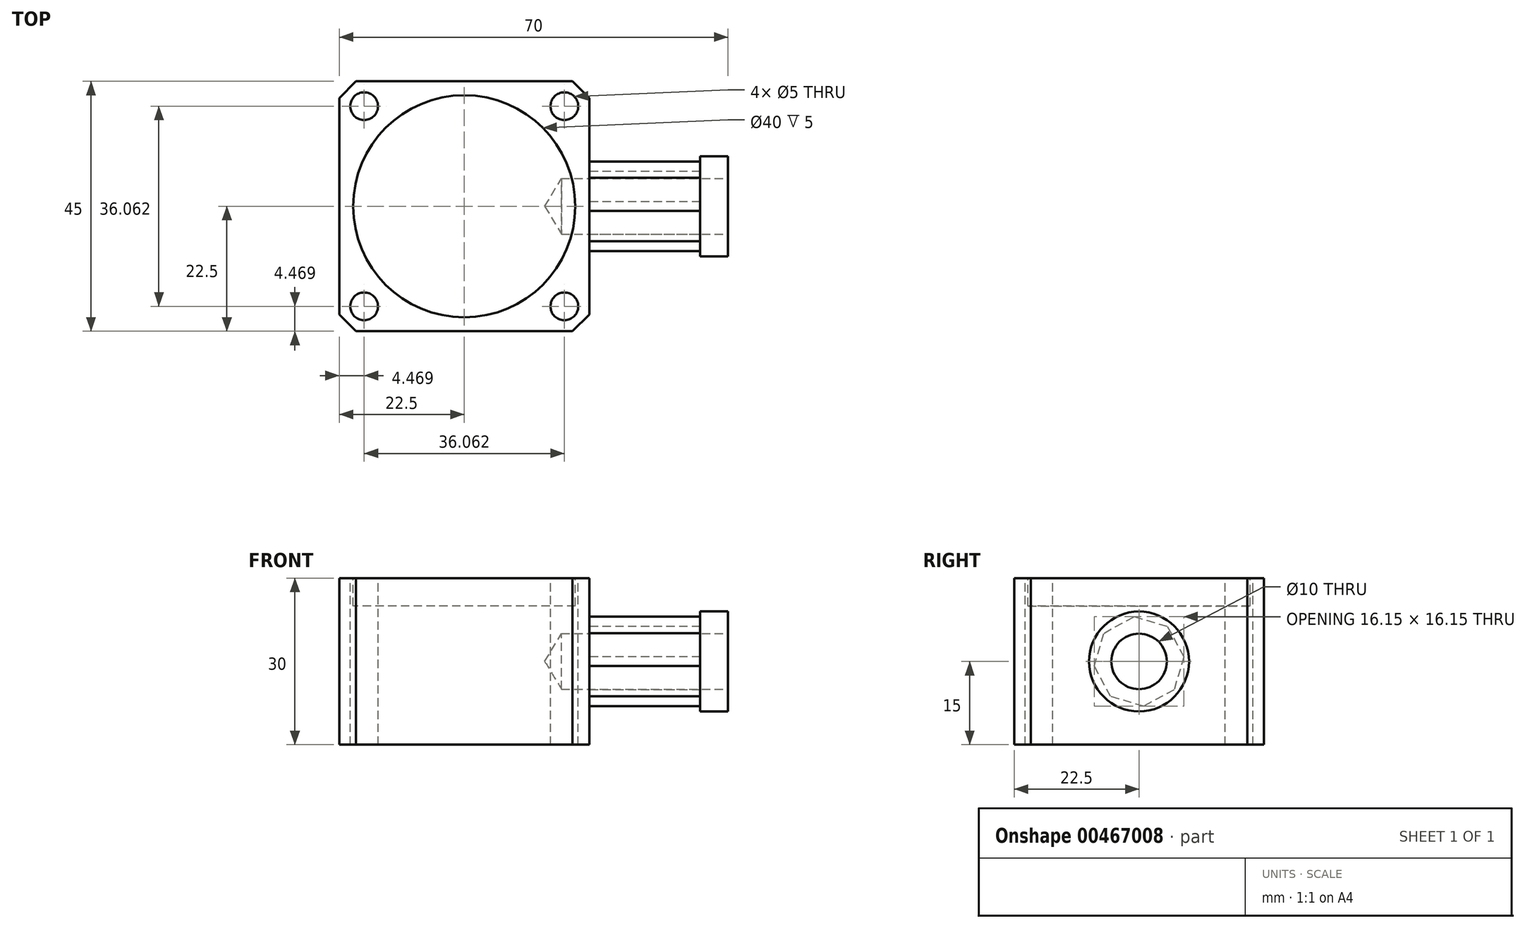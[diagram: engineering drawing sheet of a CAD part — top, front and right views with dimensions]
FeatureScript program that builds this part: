
annotation { "Feature Type Name" : "Feature", "Feature Type Description" : "" }
export const myFeature = defineFeature(function(context is Context, id is Id, definition is map)
    precondition{}
    {
        {
            var Q0;
            Q0=qCreatedBy(makeId("Top.planeOp"),FACE);
            var sketch = newSketch(context, id + "F0", { "sketchPlane" : qUnion([Q0])});
            skLineSegment(sketch, "E0.bottom", {"start": v(0, 0) * mm, "end": v(-45, 0) * mm});
            skLineSegment(sketch, "E0.top", {"start": v(0, -45) * mm, "end": v(-45, -45) * mm});
            skLineSegment(sketch, "E0.left", {"start": v(0, 0) * mm, "end": v(0, -45) * mm});
            skLineSegment(sketch, "E0.right", {"start": v(-45, 0) * mm, "end": v(-45, -45) * mm});
            skSolve(sketch);
        }
        {
            var Q0;
            Q0=makeQuery(id+"F0.imprint","IMPRINT",FACE,{"disambiguationData":[TD([[makeQuery(id+"F0.imprint","IMPRINT",EDGE,{"derivedFrom":sQuery(id+"F0.wireOp",EDGE,"E0.bottom")}),1.0]])]});
            extrude(context, id + "F1", {"entities" : qUnion([Q0]), "depth" : 30 * mm, "offsetDistance" : 25 * mm});
        }
        {
            var Q0;
            Q0=makeQuery(id+"F1.opExtrude","SWEPT_EDGE",EDGE,{"disambiguationData":[OSD([sQuery(id+"F0.wireOp",EDGE,"E0.top"),sQuery(id+"F0.wireOp",EDGE,"E0.right")])]});
            var Q1;
            Q1=makeQuery(id+"F1.opExtrude","SWEPT_EDGE",EDGE,{"disambiguationData":[OSD([sQuery(id+"F0.wireOp",EDGE,"E0.top"),sQuery(id+"F0.wireOp",EDGE,"E0.left")])]});
            var Q2;
            Q2=makeQuery(id+"F1.opExtrude","SWEPT_EDGE",EDGE,{"disambiguationData":[OSD([sQuery(id+"F0.wireOp",EDGE,"E0.bottom"),sQuery(id+"F0.wireOp",EDGE,"E0.left")])]});
            var Q3;
            Q3=makeQuery(id+"F1.opExtrude","SWEPT_EDGE",EDGE,{"disambiguationData":[OSD([sQuery(id+"F0.wireOp",EDGE,"E0.bottom"),sQuery(id+"F0.wireOp",EDGE,"E0.right")])]});
            chamfer(context, id + "F2", {"entities" : qUnion([Q0, Q1, Q2, Q3]), "width" : 3 * mm, "tangentPropagation" : true});
        }
        {
            var Q0;
            Q0=makeQuery(id+"F1.opExtrude","CAP_FACE",FACE,{"disambiguationData":[OSD([sQuery(id+"F0.wireOp",EDGE,"E0.bottom"),sQuery(id+"F0.wireOp",EDGE,"E0.top"),sQuery(id+"F0.wireOp",EDGE,"E0.left"),sQuery(id+"F0.wireOp",EDGE,"E0.right")])],"isStart":false});
            var sketch = newSketch(context, id + "F3", { "sketchPlane" : qUnion([Q0])});
            skLineSegment(sketch, "E1", {"start": v(-22.5, -22.5) * mm, "end": v(0, -22.5) * mm});
            skPoint(sketch, "E1.startSnap0", {"position": v(-22.5, -3) * mm});
            skPoint(sketch, "E1.startSnap1", {"position": v(0, -22.5) * mm});
            skLineSegment(sketch, "E2", {"start": v(0, -22.5) * mm, "end": v(-22.5, -22.5) * mm});
            skLineSegment(sketch, "E3", {"start": v(-22.5, -22.5) * mm, "end": v(-40.53, -40.53) * mm});
            skLineSegment(sketch, "E4.MirrorCS", {"start": v(-22.5, -22.5) * mm, "end": v(-40.53, -4.47) * mm});
            skPoint(sketch, "E5", {"position": v(-40.53, -40.53) * mm});
            skPoint(sketch, "E6", {"position": v(-40.53, -4.47) * mm});
            skLineSegment(sketch, "E7", {"start": v(-22.5, -22.5) * mm, "end": v(-4.47, -4.47) * mm});
            skLineSegment(sketch, "E8.MirrorCS", {"start": v(-22.5, -22.5) * mm, "end": v(-4.47, -40.53) * mm});
            skPoint(sketch, "E9", {"position": v(-4.47, -4.47) * mm});
            skPoint(sketch, "E10", {"position": v(-4.47, -40.53) * mm});
            skSolve(sketch);
        }
        {
            var Q0;
            Q0=sQuery(id+"F3.wireOp",VERTEX,"E5");
            var Q1;
            Q1=sQuery(id+"F3.wireOp",VERTEX,"E6");
            var Q2;
            Q2=sQuery(id+"F3.wireOp",VERTEX,"E9");
            var Q3;
            Q3=sQuery(id+"F3.wireOp",VERTEX,"E10");
            var Q4;
            Q4=makeQuery(id+"F1.opExtrude","SWEPT_BODY",BODY,{"disambiguationData":[OSD([sQuery(id+"F0.wireOp",EDGE,"E0.bottom"),sQuery(id+"F0.wireOp",EDGE,"E0.top"),sQuery(id+"F0.wireOp",EDGE,"E0.left"),sQuery(id+"F0.wireOp",EDGE,"E0.right")])]});
            hole(context, id + "F4", {"style" : HoleStyle.SIMPLE, "endStyle" : HoleEndStyle.THROUGH, "holeDiameter" : 5 * mm, "isTappedThrough" : true, "tappedDepth" : 12 * mm, "tapClearance" : 3, "locations" : qUnion([Q0, Q1, Q2, Q3]), "scope" : qUnion([Q4])});
        }
        {
            var Q0;
            Q0=makeQuery(id+"F1.opExtrude","SWEPT_FACE",FACE,{"disambiguationData":[OSD([sQuery(id+"F0.wireOp",EDGE,"E0.left")])]});
            var sketch = newSketch(context, id + "F5", { "sketchPlane" : qUnion([Q0])});
            skCircle(sketch, "E11", {"center": v(-22.5, 15) * mm, "radius": 7.5 * mm});
            skPoint(sketch, "E11.centerSnap0", {"position": v(-42, 15) * mm});
            skPoint(sketch, "E11.centerSnap1", {"position": v(-22.5, 30) * mm});
            skCircle(sketch, "E12.cCircle", {"center": v(-22.5, 15) * mm, "radius": 7.5 * mm, "construction": true});
            skLineSegment(sketch, "E12.0", {"start": v(-30.57, 14.16) * mm, "end": v(-28.8, 20.12) * mm});
            skLineSegment(sketch, "E12.1", {"start": v(-28.8, 20.12) * mm, "end": v(-23.34, 23.07) * mm});
            skLineSegment(sketch, "E12.2", {"start": v(-23.34, 23.07) * mm, "end": v(-17.38, 21.3) * mm});
            skLineSegment(sketch, "E12.3", {"start": v(-17.38, 21.3) * mm, "end": v(-14.43, 15.84) * mm});
            skLineSegment(sketch, "E12.4", {"start": v(-14.43, 15.84) * mm, "end": v(-16.2, 9.88) * mm});
            skLineSegment(sketch, "E12.5", {"start": v(-16.2, 9.88) * mm, "end": v(-21.66, 6.93) * mm});
            skLineSegment(sketch, "E12.6", {"start": v(-21.66, 6.93) * mm, "end": v(-27.62, 8.7) * mm});
            skLineSegment(sketch, "E12.7", {"start": v(-27.62, 8.7) * mm, "end": v(-30.57, 14.16) * mm});
            skPoint(sketch, "E12.0.midPoint", {"position": v(-29.69, 17.14) * mm});
            skSolve(sketch);
        }
        {
            var Q0;
            Q0 = qSketchRegion(id + "F5", true);
            extrude(context, id + "F6", {"entities" : qUnion([Q0]), "operationType" : NewBodyOperationType.ADD, "depth" : 20 * mm});
        }
        {
            var Q0;
            Q0=makeQuery(id+"F6.opExtrude","CAP_FACE",FACE,{"disambiguationData":[OSD([sQuery(id+"F5.wireOp",EDGE,"E12.0"),sQuery(id+"F5.wireOp",EDGE,"E12.1"),sQuery(id+"F5.wireOp",EDGE,"E12.2"),sQuery(id+"F5.wireOp",EDGE,"E12.3"),sQuery(id+"F5.wireOp",EDGE,"E12.4"),sQuery(id+"F5.wireOp",EDGE,"E12.5"),sQuery(id+"F5.wireOp",EDGE,"E12.6"),sQuery(id+"F5.wireOp",EDGE,"E12.7")])],"isStart":false});
            var sketch = newSketch(context, id + "F7", { "sketchPlane" : qUnion([Q0])});
            skLineSegment(sketch, "E13", {"start": v(-20.36, 22.19) * mm, "end": v(-24.64, 7.81) * mm});
            skLineSegment(sketch, "E14", {"start": v(-24.64, 7.81) * mm, "end": v(-29.69, 17.14) * mm});
            skLineSegment(sketch, "E15", {"start": v(-29.69, 17.14) * mm, "end": v(-15.31, 12.86) * mm});
            skCircle(sketch, "E16", {"center": v(-22.5, 15) * mm, "radius": 9 * mm});
            skSolve(sketch);
        }
        {
            var Q0;
            Q0 = qSketchRegion(id + "F7", true);
            var Q1;
            {var subQ0=sQuery(id+"F7.wireOp",EDGE,"E14");Q1=makeQuery(id+"F7.imprint","IMPRINT",FACE,{"disambiguationData":[TD([[makeQuery(id+"F7.imprint","IMPRINT",EDGE,{"derivedFrom":subQ0}),-1.0]])]});}
            extrude(context, id + "F8", {"entities" : qUnion([Q0, Q1]), "operationType" : NewBodyOperationType.ADD, "depth" : 5 * mm});
        }
        {
            var Q0;
            Q0=makeQuery(id+"F8.opExtrude","CAP_FACE",FACE,{"disambiguationData":[OSD([sQuery(id+"F7.wireOp",EDGE,"E16")])],"isStart":false});
            var sketch = newSketch(context, id + "F9", { "sketchPlane" : qUnion([Q0])});
            skPoint(sketch, "E17", {"position": v(-22.5, 15) * mm});
            skSolve(sketch);
        }
        {
            var Q0;
            Q0=sQuery(id+"F9.wireOp",VERTEX,"E17");
            var Q1;
            Q1=makeQuery(id+"F1.opExtrude","SWEPT_BODY",BODY,{"disambiguationData":[OSD([sQuery(id+"F0.wireOp",EDGE,"E0.bottom"),sQuery(id+"F0.wireOp",EDGE,"E0.top"),sQuery(id+"F0.wireOp",EDGE,"E0.left"),sQuery(id+"F0.wireOp",EDGE,"E0.right")])]});
            hole(context, id + "F10", {"style" : HoleStyle.SIMPLE, "endStyle" : HoleEndStyle.BLIND, "holeDiameter" : 10 * mm, "holeDepth" : 30 * mm, "isTappedThrough" : true, "tappedDepth" : 12 * mm, "tapClearance" : 3, "locations" : qUnion([Q0]), "scope" : qUnion([Q1])});
        }
        {
            var Q0;
            Q0=makeQuery(id+"F1.opExtrude","CAP_FACE",FACE,{"disambiguationData":[OSD([sQuery(id+"F0.wireOp",EDGE,"E0.bottom"),sQuery(id+"F0.wireOp",EDGE,"E0.top"),sQuery(id+"F0.wireOp",EDGE,"E0.left"),sQuery(id+"F0.wireOp",EDGE,"E0.right")])],"isStart":false});
            var sketch = newSketch(context, id + "F11", { "sketchPlane" : qUnion([Q0])});
            skCircle(sketch, "E18", {"center": v(-22.5, -22.5) * mm, "radius": 20 * mm});
            skPoint(sketch, "E18.centerSnap0", {"position": v(-45, -22.5) * mm});
            skPoint(sketch, "E18.centerSnap1", {"position": v(-22.5, -42) * mm});
            skSolve(sketch);
        }
        {
            var Q0;
            Q0=makeQuery(id+"F11.imprint","IMPRINT",FACE,{"disambiguationData":[TD([[makeQuery(id+"F11.imprint","IMPRINT",EDGE,{"derivedFrom":sQuery(id+"F11.wireOp",EDGE,"E18")}),1.0]])]});
            extrude(context, id + "F12", {"entities" : qUnion([Q0]), "operationType" : NewBodyOperationType.REMOVE, "oppositeDirection" : true, "depth" : 5 * mm});
        }
    });
